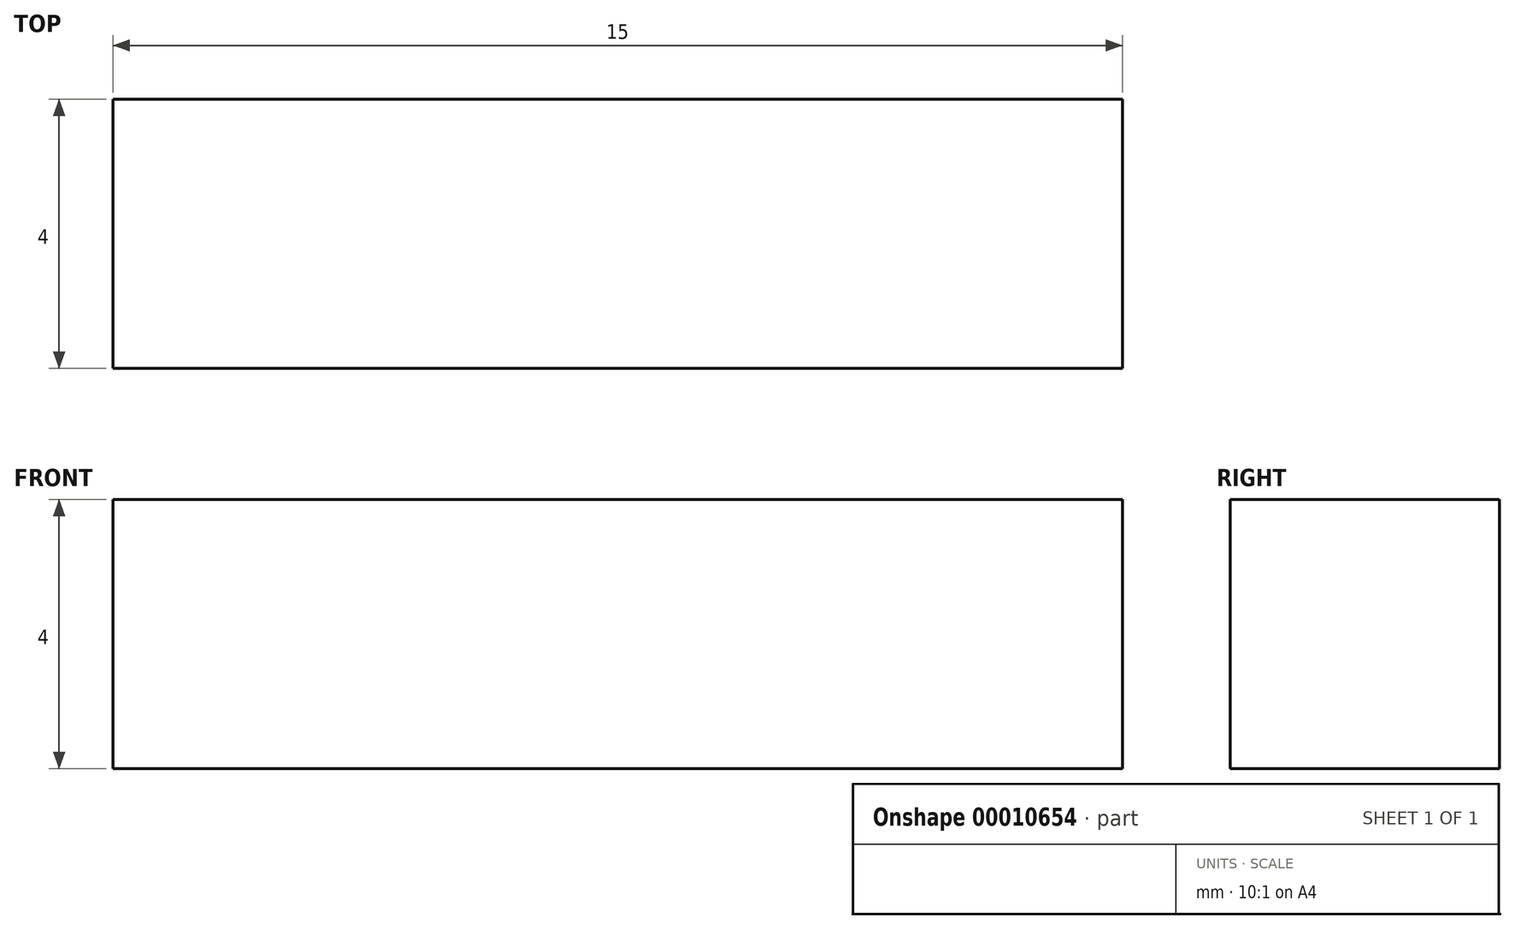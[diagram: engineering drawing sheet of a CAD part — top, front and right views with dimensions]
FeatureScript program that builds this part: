
annotation { "Feature Type Name" : "Feature", "Feature Type Description" : "" }
export const myFeature = defineFeature(function(context is Context, id is Id, definition is map)
    precondition{}
    {
        {
            var Q0;
            Q0=qCreatedBy(makeId("Front.planeOp"),FACE);
            var sketch = newSketch(context, id + "F0", { "sketchPlane" : qUnion([Q0])});
            skLineSegment(sketch, "E0.bottom", {"start": v(0, 0) * mm, "end": v(-15, 0) * mm});
            skLineSegment(sketch, "E0.top", {"start": v(0, -4) * mm, "end": v(-15, -4) * mm});
            skLineSegment(sketch, "E0.left", {"start": v(0, 0) * mm, "end": v(0, -4) * mm});
            skLineSegment(sketch, "E0.right", {"start": v(-15, 0) * mm, "end": v(-15, -4) * mm});
            skSolve(sketch);
        }
        {
            var Q0;
            Q0=makeQuery(id+"F0.imprint","IMPRINT",FACE,{"disambiguationData":[TD([[makeQuery(id+"F0.imprint","IMPRINT",EDGE,{"derivedFrom":sQuery(id+"F0.wireOp",EDGE,"E0.bottom")}),1.0]])]});
            extrude(context, id + "F1", {"entities" : qUnion([Q0]), "depth" : 4 * mm});
        }
    });
